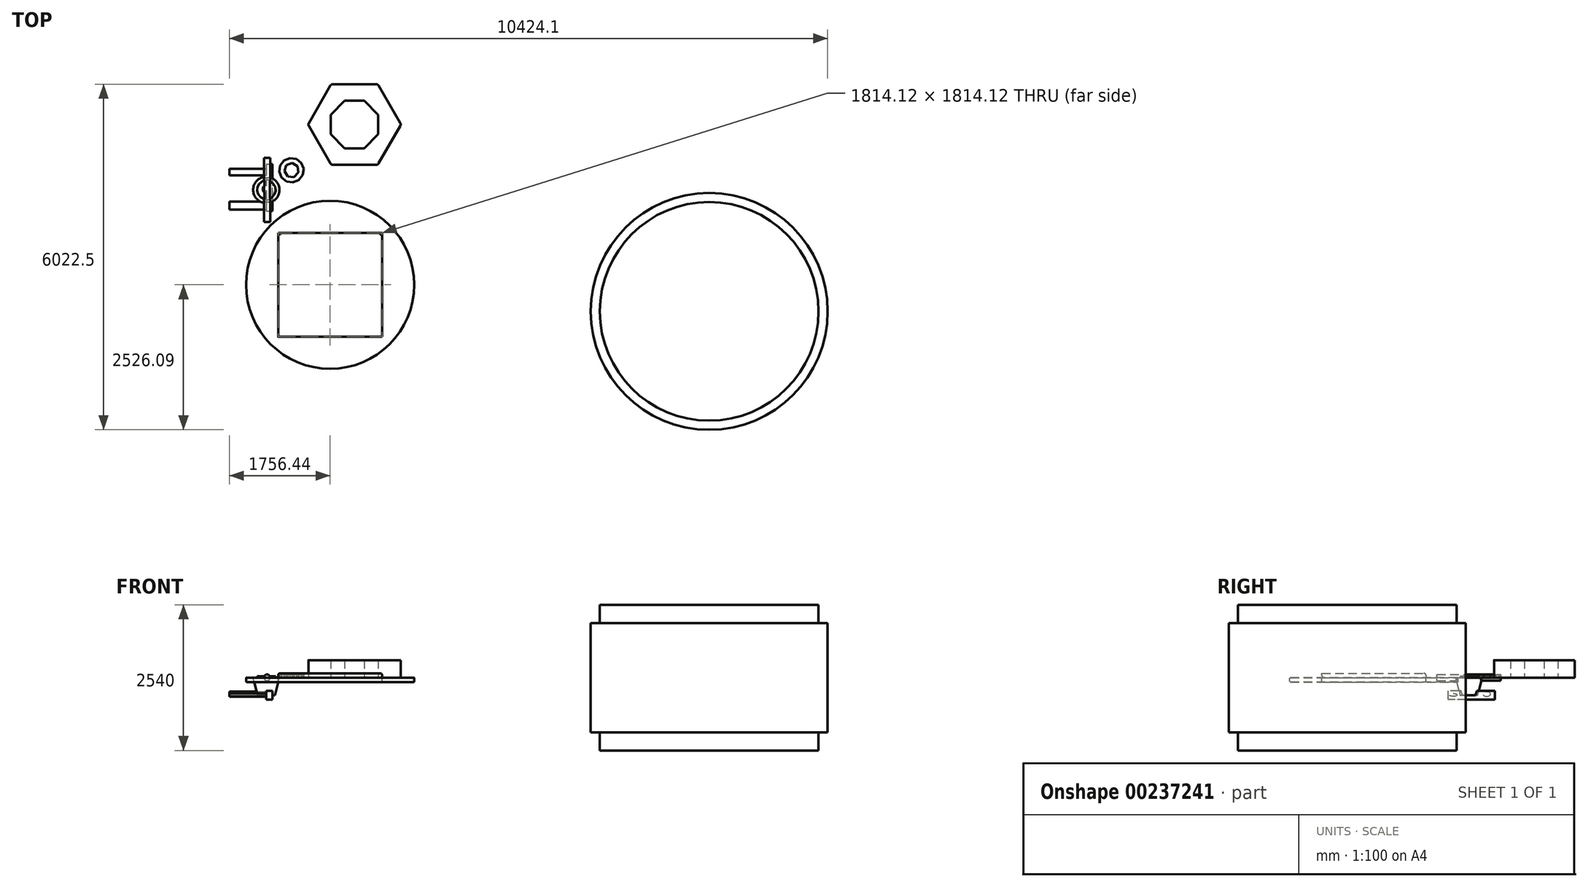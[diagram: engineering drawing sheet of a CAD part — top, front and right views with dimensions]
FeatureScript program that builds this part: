
annotation { "Feature Type Name" : "Feature", "Feature Type Description" : "" }
export const myFeature = defineFeature(function(context is Context, id is Id, definition is map)
    precondition{}
    {
        {
            var Q0;
            Q0=qCreatedBy(makeId("Top.planeOp"),FACE);
            var sketch = newSketch(context, id + "F0", { "sketchPlane" : qUnion([Q0])});
            skCircle(sketch, "E0.cCircle", {"center": v(0, 0) * mm, "radius": 162.75 * mm, "construction": true});
            skLineSegment(sketch, "E0.0", {"start": v(122.54, 107.1) * mm, "end": v(155.5, 48) * mm});
            skLineSegment(sketch, "E0.1", {"start": v(155.5, 48) * mm, "end": v(161.59, -19.4) * mm});
            skLineSegment(sketch, "E0.2", {"start": v(161.59, -19.4) * mm, "end": v(139.72, -83.45) * mm});
            skLineSegment(sketch, "E0.3", {"start": v(139.72, -83.45) * mm, "end": v(93.7, -133.07) * mm});
            skLineSegment(sketch, "E0.4", {"start": v(93.7, -133.07) * mm, "end": v(31.48, -159.67) * mm});
            skLineSegment(sketch, "E0.5", {"start": v(31.48, -159.67) * mm, "end": v(-36.19, -158.67) * mm});
            skLineSegment(sketch, "E0.6", {"start": v(-36.19, -158.67) * mm, "end": v(-97.6, -130.23) * mm});
            skLineSegment(sketch, "E0.7", {"start": v(-97.6, -130.23) * mm, "end": v(-142.13, -79.28) * mm});
            skLineSegment(sketch, "E0.8", {"start": v(-142.13, -79.28) * mm, "end": v(-162.09, -14.61) * mm});
            skLineSegment(sketch, "E0.9", {"start": v(-162.09, -14.61) * mm, "end": v(-154.02, 52.58) * mm});
            skLineSegment(sketch, "E0.10", {"start": v(-154.02, 52.58) * mm, "end": v(-119.32, 110.68) * mm});
            skLineSegment(sketch, "E0.11", {"start": v(-119.32, 110.68) * mm, "end": v(-63.99, 149.64) * mm});
            skLineSegment(sketch, "E0.12", {"start": v(-63.99, 149.64) * mm, "end": v(2.4, 162.73) * mm});
            skLineSegment(sketch, "E0.13", {"start": v(2.4, 162.73) * mm, "end": v(68.39, 147.68) * mm});
            skLineSegment(sketch, "E0.14", {"start": v(68.39, 147.68) * mm, "end": v(122.54, 107.1) * mm});
            skCircle(sketch, "E1.cCircle", {"center": v(0, 13.94) * mm, "radius": 64 * mm, "construction": true});
            skLineSegment(sketch, "E1.0", {"start": v(63.59, 21.28) * mm, "end": v(50.15, -25.83) * mm});
            skLineSegment(sketch, "E1.1", {"start": v(50.15, -25.83) * mm, "end": v(7.34, -49.65) * mm});
            skLineSegment(sketch, "E1.2", {"start": v(7.34, -49.65) * mm, "end": v(-39.77, -36.22) * mm});
            skLineSegment(sketch, "E1.3", {"start": v(-39.77, -36.22) * mm, "end": v(-63.59, 6.6) * mm});
            skLineSegment(sketch, "E1.4", {"start": v(-63.59, 6.6) * mm, "end": v(-50.15, 53.7) * mm});
            skLineSegment(sketch, "E1.5", {"start": v(-50.15, 53.7) * mm, "end": v(-7.34, 77.52) * mm});
            skLineSegment(sketch, "E1.6", {"start": v(-7.34, 77.52) * mm, "end": v(39.77, 64.09) * mm});
            skLineSegment(sketch, "E1.7", {"start": v(39.77, 64.09) * mm, "end": v(63.59, 21.28) * mm});
            skSolve(sketch);
        }
        {
            var Q0;
            Q0=makeQuery(id+"F0.imprint","IMPRINT",FACE,{"disambiguationData":[TD([[makeQuery(id+"F0.imprint","IMPRINT",EDGE,{"derivedFrom":sQuery(id+"F0.wireOp",EDGE,"E0.0")}),-1.0]])]});
            extrude(context, id + "F1", {"entities" : qUnion([Q0]), "depth" : 25.4 * mm});
        }
        {
            var Q0;
            Q0=qCreatedBy(makeId("Top.planeOp"),FACE);
            var sketch = newSketch(context, id + "F2", { "sketchPlane" : qUnion([Q0])});
            skCircle(sketch, "E2.cCircle", {"center": v(439.67, 342.5) * mm, "radius": 212.8 * mm, "construction": true});
            skLineSegment(sketch, "E2.0", {"start": v(635.27, 258.7) * mm, "end": v(567.16, 172.12) * mm});
            skLineSegment(sketch, "E2.1", {"start": v(567.16, 172.12) * mm, "end": v(464.89, 131.2) * mm});
            skLineSegment(sketch, "E2.2", {"start": v(464.89, 131.2) * mm, "end": v(355.86, 146.9) * mm});
            skLineSegment(sketch, "E2.3", {"start": v(355.86, 146.9) * mm, "end": v(269.29, 215.01) * mm});
            skLineSegment(sketch, "E2.4", {"start": v(269.29, 215.01) * mm, "end": v(228.37, 317.28) * mm});
            skLineSegment(sketch, "E2.5", {"start": v(228.37, 317.28) * mm, "end": v(244.07, 426.31) * mm});
            skLineSegment(sketch, "E2.6", {"start": v(244.07, 426.31) * mm, "end": v(312.18, 512.89) * mm});
            skLineSegment(sketch, "E2.7", {"start": v(312.18, 512.89) * mm, "end": v(414.45, 553.8) * mm});
            skLineSegment(sketch, "E2.8", {"start": v(414.45, 553.8) * mm, "end": v(523.48, 538.1) * mm});
            skLineSegment(sketch, "E2.9", {"start": v(523.48, 538.1) * mm, "end": v(610.05, 470) * mm});
            skLineSegment(sketch, "E2.10", {"start": v(610.05, 470) * mm, "end": v(650.97, 367.72) * mm});
            skLineSegment(sketch, "E2.11", {"start": v(650.97, 367.72) * mm, "end": v(635.27, 258.7) * mm});
            skCircle(sketch, "E3.cCircle", {"center": v(439.67, 342.5) * mm, "radius": 125.31 * mm, "construction": true});
            skLineSegment(sketch, "E3.0", {"start": v(558.33, 302.22) * mm, "end": v(482.16, 224.62) * mm});
            skLineSegment(sketch, "E3.1", {"start": v(482.16, 224.62) * mm, "end": v(374, 235.78) * mm});
            skLineSegment(sketch, "E3.2", {"start": v(374, 235.78) * mm, "end": v(315.28, 327.3) * mm});
            skLineSegment(sketch, "E3.3", {"start": v(315.28, 327.3) * mm, "end": v(350.23, 430.28) * mm});
            skLineSegment(sketch, "E3.4", {"start": v(350.23, 430.28) * mm, "end": v(452.53, 467.15) * mm});
            skLineSegment(sketch, "E3.5", {"start": v(452.53, 467.15) * mm, "end": v(545.14, 410.16) * mm});
            skLineSegment(sketch, "E3.6", {"start": v(545.14, 410.16) * mm, "end": v(558.33, 302.22) * mm});
            skSolve(sketch);
        }
        {
            var Q0;
            Q0=makeQuery(id+"F2.imprint","IMPRINT",FACE,{"disambiguationData":[TD([[makeQuery(id+"F2.imprint","IMPRINT",EDGE,{"derivedFrom":sQuery(id+"F2.wireOp",EDGE,"E2.0")}),-1.0]])]});
            extrude(context, id + "F3", {"entities" : qUnion([Q0]), "depth" : 51.3 * mm});
        }
        {
            var Q0;
            Q0=qCreatedBy(makeId("Top.planeOp"),FACE);
            var sketch = newSketch(context, id + "F4", { "sketchPlane" : qUnion([Q0])});
            skCircle(sketch, "E4.cCircle", {"center": v(1538.2, 1139.56) * mm, "radius": 810.97 * mm, "construction": true});
            skLineSegment(sketch, "E4.0", {"start": v(2349.16, 1139.56) * mm, "end": v(1943.68, 437.24) * mm});
            skLineSegment(sketch, "E4.1", {"start": v(1943.68, 437.24) * mm, "end": v(1132.71, 437.24) * mm});
            skLineSegment(sketch, "E4.2", {"start": v(1132.71, 437.24) * mm, "end": v(727.23, 1139.56) * mm});
            skLineSegment(sketch, "E4.3", {"start": v(727.23, 1139.56) * mm, "end": v(1132.71, 1841.87) * mm});
            skLineSegment(sketch, "E4.4", {"start": v(1132.71, 1841.87) * mm, "end": v(1943.68, 1841.87) * mm});
            skLineSegment(sketch, "E4.5", {"start": v(1943.68, 1841.87) * mm, "end": v(2349.16, 1139.56) * mm});
            skCircle(sketch, "E5.cCircle", {"center": v(1538.2, 1139.56) * mm, "radius": 447.1 * mm, "construction": true});
            skLineSegment(sketch, "E5.0", {"start": v(1951.26, 1310.66) * mm, "end": v(1951.26, 968.46) * mm});
            skLineSegment(sketch, "E5.1", {"start": v(1951.26, 968.46) * mm, "end": v(1709.3, 726.49) * mm});
            skLineSegment(sketch, "E5.2", {"start": v(1709.3, 726.49) * mm, "end": v(1367.1, 726.49) * mm});
            skLineSegment(sketch, "E5.3", {"start": v(1367.1, 726.49) * mm, "end": v(1125.13, 968.46) * mm});
            skLineSegment(sketch, "E5.4", {"start": v(1125.13, 968.46) * mm, "end": v(1125.13, 1310.66) * mm});
            skLineSegment(sketch, "E5.5", {"start": v(1125.13, 1310.66) * mm, "end": v(1367.1, 1552.63) * mm});
            skLineSegment(sketch, "E5.6", {"start": v(1367.1, 1552.63) * mm, "end": v(1709.3, 1552.63) * mm});
            skLineSegment(sketch, "E5.7", {"start": v(1709.3, 1552.63) * mm, "end": v(1951.26, 1310.66) * mm});
            skSolve(sketch);
        }
        {
            var Q0;
            Q0=makeQuery(id+"F4.imprint","IMPRINT",FACE,{"disambiguationData":[TD([[makeQuery(id+"F4.imprint","IMPRINT",EDGE,{"derivedFrom":sQuery(id+"F4.wireOp",EDGE,"E4.0")}),-1.0]])]});
            extrude(context, id + "F5", {"entities" : qUnion([Q0]), "depth" : 305.1 * mm});
        }
        {
            var Q0;
            Q0=makeQuery(id+"F5.opExtrude","SWEPT_EDGE",EDGE,{"disambiguationData":[OSD([sQuery(id+"F4.wireOp",EDGE,"E4.0"),sQuery(id+"F4.wireOp",EDGE,"E4.1")])]});
            var Q1;
            Q1=makeQuery(id+"F5.opExtrude","SWEPT_EDGE",EDGE,{"disambiguationData":[OSD([sQuery(id+"F4.wireOp",EDGE,"E4.0"),sQuery(id+"F4.wireOp",EDGE,"E4.5")])]});
            var Q2;
            Q2=makeQuery(id+"F5.opExtrude","SWEPT_EDGE",EDGE,{"disambiguationData":[OSD([sQuery(id+"F4.wireOp",EDGE,"E4.4"),sQuery(id+"F4.wireOp",EDGE,"E4.5")])]});
            var Q3;
            Q3=makeQuery(id+"F5.opExtrude","SWEPT_EDGE",EDGE,{"disambiguationData":[OSD([sQuery(id+"F4.wireOp",EDGE,"E4.3"),sQuery(id+"F4.wireOp",EDGE,"E4.4")])]});
            var Q4;
            Q4=makeQuery(id+"F5.opExtrude","SWEPT_EDGE",EDGE,{"disambiguationData":[OSD([sQuery(id+"F4.wireOp",EDGE,"E4.2"),sQuery(id+"F4.wireOp",EDGE,"E4.3")])]});
            var Q5;
            Q5=makeQuery(id+"F5.opExtrude","SWEPT_EDGE",EDGE,{"disambiguationData":[OSD([sQuery(id+"F4.wireOp",EDGE,"E4.1"),sQuery(id+"F4.wireOp",EDGE,"E4.2")])]});
            fillet(context, id + "F6", {"entities" : qUnion([Q0, Q1, Q2, Q3, Q4, Q5]), "radius" : 45.72 * mm, "tangentPropagation" : true, "allowEdgeOverflow" : false});
        }
        {
            var Q0;
            Q0=qCreatedBy(makeId("Top.planeOp"),FACE);
            var sketch = newSketch(context, id + "F7", { "sketchPlane" : qUnion([Q0])});
            skLineSegment(sketch, "E6.bottom", {"start": v(2020, -2561.6) * mm, "end": v(205.88, -2561.6) * mm});
            skLineSegment(sketch, "E6.top", {"start": v(2020, -747.49) * mm, "end": v(205.88, -747.49) * mm});
            skLineSegment(sketch, "E6.left", {"start": v(2020, -2561.6) * mm, "end": v(2020, -747.49) * mm});
            skLineSegment(sketch, "E6.right", {"start": v(205.88, -2561.6) * mm, "end": v(205.88, -747.49) * mm});
            skPoint(sketch, "E6.middle", {"position": v(1112.94, -1654.54) * mm});
            skCircle(sketch, "E7", {"center": v(1112.94, -1654.54) * mm, "radius": 1465.04 * mm});
            skSolve(sketch);
        }
        {
            var Q0;
            Q0=makeQuery(id+"F7.imprint","IMPRINT",FACE,{"disambiguationData":[TD([[makeQuery(id+"F7.imprint","IMPRINT",EDGE,{"derivedFrom":sQuery(id+"F7.wireOp",EDGE,"E6.bottom")}),1.0]])]});
            extrude(context, id + "F8", {"entities" : qUnion([Q0]), "oppositeDirection" : true, "depth" : 76.2 * mm});
        }
        {
            var Q0;
            Q0=makeQuery(id+"F7.imprint","IMPRINT",FACE,{"disambiguationData":[TD([[makeQuery(id+"F7.imprint","IMPRINT",EDGE,{"derivedFrom":sQuery(id+"F7.wireOp",EDGE,"E6.bottom")}),-1.0]])]});
            extrude(context, id + "F9", {"entities" : qUnion([Q0]), "depth" : 76.2 * mm});
        }
        {
            var Q0;
            Q0=makeQuery(id+"F9.opExtrude","CAP_EDGE",EDGE,{"disambiguationData":[OSD([sQuery(id+"F7.wireOp",EDGE,"E6.right")])],"isStart":false});
            var Q1;
            Q1=makeQuery(id+"F9.opExtrude","CAP_EDGE",EDGE,{"disambiguationData":[OSD([sQuery(id+"F7.wireOp",EDGE,"E6.left")])],"isStart":false});
            var Q2;
            Q2=makeQuery(id+"F9.opExtrude","CAP_EDGE",EDGE,{"disambiguationData":[OSD([sQuery(id+"F7.wireOp",EDGE,"E6.bottom")])],"isStart":true});
            var Q3;
            Q3=makeQuery(id+"F9.opExtrude","CAP_EDGE",EDGE,{"disambiguationData":[OSD([sQuery(id+"F7.wireOp",EDGE,"E6.top")])],"isStart":false});
            fillet(context, id + "F10", {"entities" : qUnion([Q0, Q1, Q2, Q3]), "radius" : 38.1 * mm, "tangentPropagation" : true, "allowEdgeOverflow" : false});
        }
        {
            var Q0;
            Q0=makeQuery(id+"F8.opExtrude","CAP_EDGE",EDGE,{"disambiguationData":[OSD([sQuery(id+"F7.wireOp",EDGE,"E7")])],"isStart":true});
            var Q1;
            Q1=makeQuery(id+"F8.opExtrude","CAP_EDGE",EDGE,{"disambiguationData":[OSD([sQuery(id+"F7.wireOp",EDGE,"E7")])],"isStart":false});
            fillet(context, id + "F11", {"entities" : qUnion([Q0, Q1]), "radius" : 12.7 * mm, "tangentPropagation" : true, "allowEdgeOverflow" : false});
        }
        {
            var Q0;
            Q0=qCreatedBy(makeId("Top.planeOp"),FACE);
            var sketch = newSketch(context, id + "F12", { "sketchPlane" : qUnion([Q0])});
            skCircle(sketch, "E8", {"center": v(7716.86, -2116.88) * mm, "radius": 1905 * mm});
            skCircle(sketch, "E9", {"center": v(7716.86, -2116.88) * mm, "radius": 2063.75 * mm});
            skSolve(sketch);
        }
        {
            var Q0;
            Q0=makeQuery(id+"F12.imprint","IMPRINT",FACE,{"disambiguationData":[TD([[makeQuery(id+"F12.imprint","IMPRINT",EDGE,{"derivedFrom":sQuery(id+"F12.wireOp",EDGE,"E8")}),1.0]])]});
            extrude(context, id + "F13", {"entities" : qUnion([Q0]), "endBound" : BoundingType.SYMMETRIC, "depth" : 2540 * mm});
        }
        {
            var Q0;
            Q0=makeQuery(id+"F12.imprint","IMPRINT",FACE,{"disambiguationData":[TD([[makeQuery(id+"F12.imprint","IMPRINT",EDGE,{"derivedFrom":sQuery(id+"F12.wireOp",EDGE,"E8")}),-1.0]])]});
            extrude(context, id + "F14", {"entities" : qUnion([Q0]), "operationType" : NewBodyOperationType.ADD, "endBound" : BoundingType.SYMMETRIC, "depth" : 1905 * mm});
        }
        {
            var Q0;
            Q0=qCreatedBy(makeId("Top.planeOp"),FACE);
            cPlane(context, id + "F15", {"entities" : qUnion([Q0]), "cplaneType" : CPlaneType.OFFSET, "offset" : 304.8 * mm, "width" : 152.4 * mm, "height" : 152.4 * mm});
        }
        {
            var Q0;
            Q0=qCreatedBy(id+"F15.planeOp",FACE);
            var sketch = newSketch(context, id + "F16", { "sketchPlane" : qUnion([Q0])});
            skCircle(sketch, "E10", {"center": v(0, 0) * mm, "radius": 59.05 * mm});
            skSolve(sketch);
        }
        {
            var Q0;
            Q0=qCreatedBy(makeId("Top.planeOp"),FACE);
            var sketch = newSketch(context, id + "F17", { "sketchPlane" : qUnion([Q0])});
            skCircle(sketch, "E11", {"center": v(7.21, 0) * mm, "radius": 135.16 * mm});
            skSolve(sketch);
        }
        {
            var Q0;
            Q0=makeQuery(id+"F17.imprint","IMPRINT",FACE,{"disambiguationData":[TD([[makeQuery(id+"F17.imprint","IMPRINT",EDGE,{"derivedFrom":sQuery(id+"F17.wireOp",EDGE,"E11")}),1.0]])]});
            var Q1;
            Q1=sQuery(id+"F17.wireOp",EDGE,"E11");
            var Q2;
            Q2=sQuery(id+"F16.wireOp",EDGE,"E10");
            loft(context, id + "F18", {"bodyType" : ToolBodyType.SURFACE, "sheetProfilesArray" : [{ "sheetProfileEntities" : qUnion([Q0]) }], "wireProfilesArray" : [{ "wireProfileEntities" : qUnion([Q1]) }, { "wireProfileEntities" : qUnion([Q2]) }]});
        }
        {
            var Q0;
            Q0=qCreatedBy(makeId("Top.planeOp"),FACE);
            var sketch = newSketch(context, id + "F19", { "sketchPlane" : qUnion([Q0])});
            skCircle(sketch, "E12", {"center": v(0, 0) * mm, "radius": 229.08 * mm});
            skSolve(sketch);
        }
        {
            var Q0;
            Q0=qCreatedBy(makeId("Top.planeOp"),FACE);
            cPlane(context, id + "F20", {"entities" : qUnion([Q0]), "cplaneType" : CPlaneType.OFFSET, "offset" : 304.8 * mm, "oppositeDirection" : true, "width" : 152.4 * mm, "height" : 152.4 * mm});
        }
        {
            var Q0;
            Q0=qCreatedBy(id+"F20.planeOp",FACE);
            var sketch = newSketch(context, id + "F21", { "sketchPlane" : qUnion([Q0])});
            skCircle(sketch, "E13", {"center": v(0, 0) * mm, "radius": 154.64 * mm});
            skSolve(sketch);
        }
        {
            var Q0;
            Q0=makeQuery(id+"F19.imprint","IMPRINT",FACE,{"disambiguationData":[TD([[makeQuery(id+"F19.imprint","IMPRINT",EDGE,{"derivedFrom":sQuery(id+"F19.wireOp",EDGE,"E12")}),1.0]])]});
            var Q1;
            Q1=makeQuery(id+"F21.imprint","IMPRINT",FACE,{"disambiguationData":[TD([[makeQuery(id+"F21.imprint","IMPRINT",EDGE,{"derivedFrom":sQuery(id+"F21.wireOp",EDGE,"E13")}),1.0]])]});
            loft(context, id + "F22", {"sheetProfilesArray" : [{ "sheetProfileEntities" : qUnion([Q0]) }, { "sheetProfileEntities" : qUnion([Q1]) }]});
        }
        {
            var Q0;
            Q0=qCreatedBy(id+"F20.planeOp",FACE);
            var sketch = newSketch(context, id + "F23", { "sketchPlane" : qUnion([Q0])});
            skLineSegment(sketch, "E14.bottom", {"start": v(0, 449.05) * mm, "end": v(104.81, 449.05) * mm});
            skLineSegment(sketch, "E14.top", {"start": v(0, -367.79) * mm, "end": v(104.81, -367.79) * mm});
            skLineSegment(sketch, "E14.left", {"start": v(0, 449.05) * mm, "end": v(0, -367.79) * mm});
            skLineSegment(sketch, "E14.right", {"start": v(104.81, 449.05) * mm, "end": v(104.81, -367.79) * mm});
            skPoint(sketch, "E14.middle", {"position": v(52.4, 40.63) * mm});
            skSolve(sketch);
        }
        {
            var Q0;
            Q0 = qSketchRegion(id + "F23", true);
            extrude(context, id + "F24", {"entities" : qUnion([Q0]), "operationType" : NewBodyOperationType.ADD, "endBound" : BoundingType.SYMMETRIC, "depth" : 152.4 * mm});
        }
        {
            var Q0;
            Q0=makeQuery(id+"F24.opExtrude","SWEPT_FACE",FACE,{"disambiguationData":[OSD([sQuery(id+"F23.wireOp",EDGE,"E14.left")])]});
            var sketch = newSketch(context, id + "F25", { "sketchPlane" : qUnion([Q0])});
            skEllipse(sketch, "E15", {"center": v(272.7, -302.16) * mm, "majorRadius": 68.02 * mm, "minorRadius": 24.74 * mm, "majorAxis": v(-1, 0)});
            skEllipse(sketch, "E16", {"center": v(-310.37, -287.26) * mm, "majorRadius": 59.3 * mm, "minorRadius": 46.6 * mm, "majorAxis": v(-1, 0)});
            skSolve(sketch);
        }
        {
            var Q0;
            Q0 = qSketchRegion(id + "F25", true);
            extrude(context, id + "F26", {"entities" : qUnion([Q0]), "operationType" : NewBodyOperationType.ADD, "depth" : 643.5 * mm});
        }
        {
            var Q0;
            Q0=qCreatedBy(makeId("Front.planeOp"),FACE);
            var sketch = newSketch(context, id + "F27", { "sketchPlane" : qUnion([Q0])});
            skCircle(sketch, "E17", {"center": v(14.37, 0) * mm, "radius": 53.9 * mm});
            skSolve(sketch);
        }
        {
            var Q0;
            Q0 = qSketchRegion(id + "F27", true);
            extrude(context, id + "F28", {"entities" : qUnion([Q0]), "operationType" : NewBodyOperationType.ADD, "endBound" : BoundingType.SYMMETRIC, "depth" : 1112.7 * mm});
        }
    });
